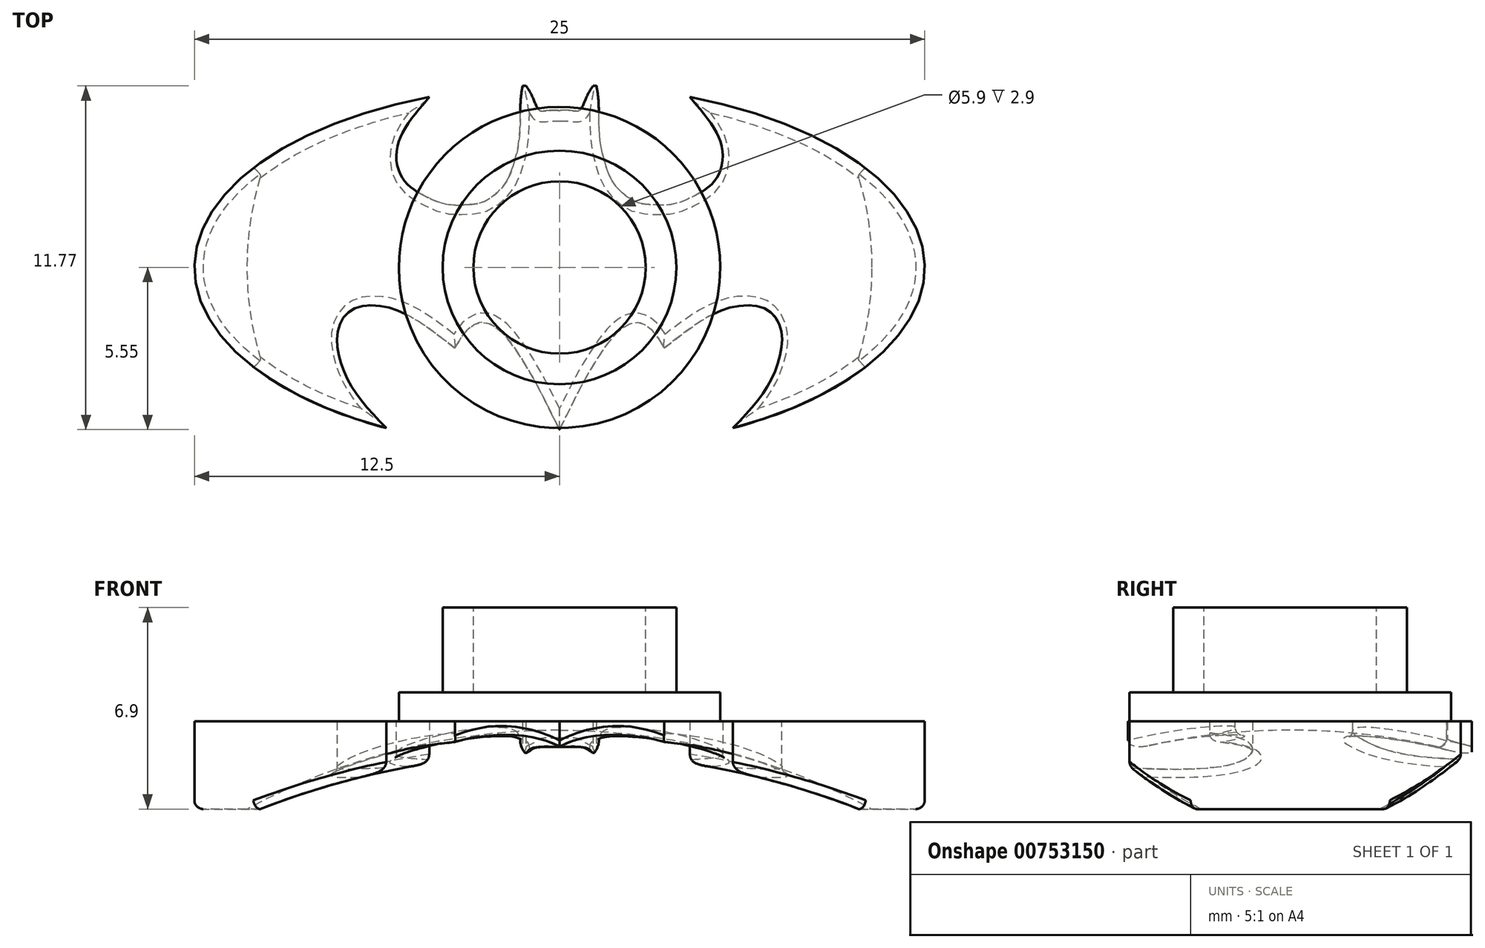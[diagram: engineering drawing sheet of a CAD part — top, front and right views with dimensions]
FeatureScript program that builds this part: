
annotation { "Feature Type Name" : "Feature", "Feature Type Description" : "" }
export const myFeature = defineFeature(function(context is Context, id is Id, definition is map)
    precondition{}
    {
        {
            var Q0;
            Q0=qCreatedBy(makeId("Top.planeOp"),FACE);
            var sketch = newSketch(context, id + "F0", { "sketchPlane" : qUnion([Q0])});
            skEllipticalArc(sketch, "E0", {});
            skFitSpline(sketch, "E1", {"points": [v(-4.46, 5.84) * mm, v(-5.29, 4.77) * mm, v(-5.59, 3.8) * mm, v(-5.32, 2.98) * mm, v(-4.7, 2.5) * mm, v(-3.86, 2.16) * mm, v(-3.2, 2.15) * mm, v(-2.63, 2.24) * mm, v(-1.92, 2.79) * mm, v(-1.58, 3.51) * mm, v(-1.38, 4.44) * mm, v(-1.34, 5.49) * mm, v(-1.26, 6.22) * mm], "startDerivative": vector(-6.9, -8.46) * mm, "endDerivative": vector(1.94, 8.78) * mm});
            skLineSegment(sketch, "E2", {"start": v(0, 0) * mm, "end": v(0, 8.48) * mm, "construction": true});
            skFitSpline(sketch, "E3", {"points": [v(-1.15, 6.22) * mm, v(-0.95, 5.9) * mm, v(-0.8, 5.56) * mm, v(-0.66, 5.36) * mm, v(-0.5, 5.36) * mm, v(-0.24, 5.38) * mm, v(0, 5.38) * mm], "startDerivative": vector(1, -1.46) * mm, "endDerivative": vector(2.36, 0) * mm});
            skLineSegment(sketch, "E4", {"start": v(0, 5.38) * mm, "end": v(0.24, 5.38) * mm, "construction": true});
            skFitSpline(sketch, "E5", {"points": [v(-5.93, -5.5) * mm, v(-6.91, -4.39) * mm, v(-7.47, -3.28) * mm, v(-7.59, -2.16) * mm, v(-7.04, -1.41) * mm, v(-5.77, -1.4) * mm, v(-4.58, -2.01) * mm, v(-3.58, -2.76) * mm], "startDerivative": vector(-6.75, 6.97) * mm, "endDerivative": vector(6.73, -5.3) * mm});
            skFitSpline(sketch, "E6", {"points": [v(0, -5.55) * mm, v(-0.77, -4.02) * mm, v(-1.45, -2.9) * mm, v(-2.1, -2.12) * mm, v(-2.72, -1.88) * mm, v(-3.26, -2.25) * mm, v(-3.58, -2.76) * mm], "startDerivative": vector(-5.35, 10.36) * mm, "endDerivative": vector(-3.6, -5.84) * mm});
            skFitSpline(sketch, "E7.MirrorCS", {"points": [v(4.46, 5.84) * mm, v(5.29, 4.77) * mm, v(5.59, 3.8) * mm, v(5.32, 2.98) * mm, v(4.7, 2.5) * mm, v(3.86, 2.16) * mm, v(3.2, 2.15) * mm, v(2.63, 2.24) * mm, v(1.92, 2.79) * mm, v(1.58, 3.51) * mm, v(1.38, 4.44) * mm, v(1.34, 5.49) * mm, v(1.26, 6.22) * mm], "startDerivative": vector(6.9, -8.46) * mm, "endDerivative": vector(-1.94, 8.78) * mm});
            skFitSpline(sketch, "E8.MirrorCS", {"points": [v(5.93, -5.5) * mm, v(6.91, -4.39) * mm, v(7.47, -3.28) * mm, v(7.59, -2.16) * mm, v(7.04, -1.41) * mm, v(5.77, -1.4) * mm, v(4.58, -2.01) * mm, v(3.58, -2.76) * mm], "startDerivative": vector(6.75, 6.97) * mm, "endDerivative": vector(-6.73, -5.3) * mm});
            skFitSpline(sketch, "E9.MirrorCS", {"points": [v(0, -5.55) * mm, v(0.77, -4.02) * mm, v(1.45, -2.9) * mm, v(2.1, -2.12) * mm, v(2.72, -1.88) * mm, v(3.26, -2.25) * mm, v(3.58, -2.76) * mm], "startDerivative": vector(5.35, 10.36) * mm, "endDerivative": vector(3.6, -5.84) * mm});
            skFitSpline(sketch, "E10.MirrorCS", {"points": [v(1.15, 6.22) * mm, v(0.95, 5.9) * mm, v(0.8, 5.56) * mm, v(0.66, 5.36) * mm, v(0.5, 5.36) * mm, v(0.24, 5.38) * mm, v(0, 5.38) * mm], "startDerivative": vector(-1, -1.46) * mm, "endDerivative": vector(-2.36, 0) * mm});
            skEllipticalArc(sketch, "E11.trimOffspring", {});
            skEllipticalArc(sketch, "E12.trimOffspring", {});
            skEllipticalArc(sketch, "E13.trimOffspring", {});
            const initialGuessF0  = {"E0": [0, 0, -1, 0, 0.0125, 0.00625, 5.077389266040888, 1.0763558123623582], "E11.trimOffspring": [0, 0, -1, 0, 0.0125, 0.00625, 4.804351116669659, 4.8136842039548124], "E12.trimOffspring": [0, 0, -1, 0, 0.0125, 0.00625, 4.611093756814567, 4.62042684409972], "E13.trimOffspring": [0, 0, -1, 0, 0.0125, 0.00625, 2.065236841227435, 4.34738869472849]};
            skSetInitialGuess(sketch, initialGuessF0);
            skSolve(sketch);
        }
        {
            var Q0;
            Q0 = qSketchRegion(id + "F0", true);
            extrude(context, id + "F1", {"entities" : qUnion([Q0]), "depth" : 3 * mm, "offsetDistance" : 25 * mm});
        }
        {
            var Q0;
            Q0=qCreatedBy(makeId("Front.planeOp"),FACE);
            var sketch = newSketch(context, id + "F2", { "sketchPlane" : qUnion([Q0])});
            skLineSegment(sketch, "E14", {"start": v(0, 0) * mm, "end": v(0, -4.5) * mm, "construction": true});
            skSolve(sketch);
        }
        {
            var Q0;
            Q0=qCreatedBy(makeId("Front.planeOp"),FACE);
            var sketch = newSketch(context, id + "F3", { "sketchPlane" : qUnion([Q0])});
            skArc(sketch, "E15", {"start": v(0, 2.7) * mm, "mid": v(-22.55, -19.85) * mm, "end": v(0, -42.4) * mm});
            skLineSegment(sketch, "E16", {"start": v(0, 2.7) * mm, "end": v(0, -42.4) * mm});
            skPoint(sketch, "E17", {"position": v(-10.7, 0) * mm});
            skSolve(sketch);
        }
        {
            var Q0;
            Q0 = qSketchRegion(id + "F3", true);
            var Q1;
            Q1=sQuery(id+"F3.wireOp",EDGE,"E16");
            revolve(context, id + "F4", {"operationType" : NewBodyOperationType.REMOVE, "surfaceOperationType" : NewSurfaceOperationType.NEW, "entities" : qUnion([Q0]), "axis" : qUnion([Q1]), "revolveType" : RevolveType.FULL, "oppositeDirection" : true});
        }
        {
            var Q0;
            Q0=makeQuery(id+"F1.opExtrude","CAP_FACE",FACE,{"disambiguationData":[OSD([sQuery(id+"F0.wireOp",EDGE,"E0"),sQuery(id+"F0.wireOp",EDGE,"E1"),sQuery(id+"F0.wireOp",EDGE,"E3"),sQuery(id+"F0.wireOp",EDGE,"E5"),sQuery(id+"F0.wireOp",EDGE,"E6"),sQuery(id+"F0.wireOp",EDGE,"E7.MirrorCS"),sQuery(id+"F0.wireOp",EDGE,"E8.MirrorCS"),sQuery(id+"F0.wireOp",EDGE,"E9.MirrorCS"),sQuery(id+"F0.wireOp",EDGE,"E10.MirrorCS"),sQuery(id+"F0.wireOp",EDGE,"E11.trimOffspring"),sQuery(id+"F0.wireOp",EDGE,"E12.trimOffspring"),sQuery(id+"F0.wireOp",EDGE,"E13.trimOffspring")])],"isStart":false});
            var sketch = newSketch(context, id + "F5", { "sketchPlane" : qUnion([Q0])});
            skCircle(sketch, "E18", {"center": v(0, 0) * mm, "radius": 5.5 * mm});
            skSolve(sketch);
        }
        {
            var Q0;
            Q0 = qSketchRegion(id + "F5", true);
            extrude(context, id + "F6", {"entities" : qUnion([Q0]), "operationType" : NewBodyOperationType.ADD, "depth" : 1 * mm, "offsetDistance" : 25 * mm});
        }
        {
            var Q0;
            Q0=makeQuery(id+"F6.opExtrude","CAP_FACE",FACE,{"disambiguationData":[OSD([sQuery(id+"F5.wireOp",EDGE,"E18")])],"isStart":false});
            var sketch = newSketch(context, id + "F7", { "sketchPlane" : qUnion([Q0])});
            skCircle(sketch, "E19", {"center": v(0, 0) * mm, "radius": 4 * mm});
            skSolve(sketch);
        }
        {
            var Q0;
            Q0 = qSketchRegion(id + "F7", true);
            extrude(context, id + "F8", {"entities" : qUnion([Q0]), "operationType" : NewBodyOperationType.ADD, "depth" : 2.9 * mm, "offsetDistance" : 25 * mm});
        }
        {
            var Q0;
            Q0=makeQuery(id+"F8.opExtrude","CAP_FACE",FACE,{"disambiguationData":[OSD([sQuery(id+"F7.wireOp",EDGE,"E19")])],"isStart":false});
            var sketch = newSketch(context, id + "F9", { "sketchPlane" : qUnion([Q0])});
            skCircle(sketch, "E20", {"center": v(0, 0) * mm, "radius": 2.95 * mm});
            skSolve(sketch);
        }
        {
            var Q0;
            Q0 = qSketchRegion(id + "F9", true);
            extrude(context, id + "F10", {"entities" : qUnion([Q0]), "operationType" : NewBodyOperationType.REMOVE, "oppositeDirection" : true, "depth" : 2.9 * mm, "offsetDistance" : 25 * mm});
        }
        {
            var Q0;
            Q0=makeQuery(id+"F1.opExtrude","CAP_EDGE",EDGE,{"disambiguationData":[OSD([sQuery(id+"F0.wireOp",EDGE,"E13.trimOffspring")])],"isStart":true});
            var Q1;
            Q1=makeQuery(id+"F4.boolean.opBoolean","INTERSECT",EDGE,{"disambiguationData":[OD(0.0)],"derivedFrom":[makeQuery(id+"F1.opExtrude","SWEPT_FACE",FACE,{"disambiguationData":[OSD([sQuery(id+"F0.wireOp",EDGE,"E13.trimOffspring")])]}),makeQuery(id+"F4.opRevolve","SWEPT_FACE",FACE,{"disambiguationData":[OSD([sQuery(id+"F3.wireOp",EDGE,"E15")])]})]});
            var Q2;
            Q2=makeQuery(id+"F4.boolean.opBoolean","INTERSECT",EDGE,{"disambiguationData":[OD(1.0)],"derivedFrom":[makeQuery(id+"F1.opExtrude","SWEPT_FACE",FACE,{"disambiguationData":[OSD([sQuery(id+"F0.wireOp",EDGE,"E13.trimOffspring")])]}),makeQuery(id+"F4.opRevolve","SWEPT_FACE",FACE,{"disambiguationData":[OSD([sQuery(id+"F3.wireOp",EDGE,"E15")])]})]});
            var Q3;
            Q3=makeQuery(id+"F4.boolean.opBoolean","INTERSECT",EDGE,{"disambiguationData":[OD(1.0)],"derivedFrom":[makeQuery(id+"F1.opExtrude","SWEPT_FACE",FACE,{"disambiguationData":[OSD([sQuery(id+"F0.wireOp",EDGE,"E0")])]}),makeQuery(id+"F4.opRevolve","SWEPT_FACE",FACE,{"disambiguationData":[OSD([sQuery(id+"F3.wireOp",EDGE,"E15")])]})]});
            var Q4;
            Q4=makeQuery(id+"F1.opExtrude","CAP_EDGE",EDGE,{"disambiguationData":[OSD([sQuery(id+"F0.wireOp",EDGE,"E0")])],"isStart":true});
            var Q5;
            Q5=makeQuery(id+"F4.boolean.opBoolean","INTERSECT",EDGE,{"disambiguationData":[OD(0.0)],"derivedFrom":[makeQuery(id+"F1.opExtrude","SWEPT_FACE",FACE,{"disambiguationData":[OSD([sQuery(id+"F0.wireOp",EDGE,"E0")])]}),makeQuery(id+"F4.opRevolve","SWEPT_FACE",FACE,{"disambiguationData":[OSD([sQuery(id+"F3.wireOp",EDGE,"E15")])]})]});
            var Q6;
            Q6=makeQuery(id+"F4.boolean.opBoolean","INTERSECT",EDGE,{"derivedFrom":[makeQuery(id+"F1.opExtrude","SWEPT_FACE",FACE,{"disambiguationData":[OSD([sQuery(id+"F0.wireOp",EDGE,"E5")])]}),makeQuery(id+"F4.opRevolve","SWEPT_FACE",FACE,{"disambiguationData":[OSD([sQuery(id+"F3.wireOp",EDGE,"E15")])]})]});
            var Q7;
            Q7=makeQuery(id+"F4.boolean.opBoolean","INTERSECT",EDGE,{"derivedFrom":[makeQuery(id+"F1.opExtrude","SWEPT_FACE",FACE,{"disambiguationData":[OSD([sQuery(id+"F0.wireOp",EDGE,"E6")])]}),makeQuery(id+"F4.opRevolve","SWEPT_FACE",FACE,{"disambiguationData":[OSD([sQuery(id+"F3.wireOp",EDGE,"E15")])]})]});
            var Q8;
            Q8=makeQuery(id+"F4.boolean.opBoolean","INTERSECT",EDGE,{"derivedFrom":[makeQuery(id+"F1.opExtrude","SWEPT_FACE",FACE,{"disambiguationData":[OSD([sQuery(id+"F0.wireOp",EDGE,"E9.MirrorCS")])]}),makeQuery(id+"F4.opRevolve","SWEPT_FACE",FACE,{"disambiguationData":[OSD([sQuery(id+"F3.wireOp",EDGE,"E15")])]})]});
            var Q9;
            Q9=makeQuery(id+"F4.boolean.opBoolean","INTERSECT",EDGE,{"derivedFrom":[makeQuery(id+"F1.opExtrude","SWEPT_FACE",FACE,{"disambiguationData":[OSD([sQuery(id+"F0.wireOp",EDGE,"E8.MirrorCS")])]}),makeQuery(id+"F4.opRevolve","SWEPT_FACE",FACE,{"disambiguationData":[OSD([sQuery(id+"F3.wireOp",EDGE,"E15")])]})]});
            var Q10;
            Q10=makeQuery(id+"F4.boolean.opBoolean","INTERSECT",EDGE,{"derivedFrom":[makeQuery(id+"F1.opExtrude","SWEPT_FACE",FACE,{"disambiguationData":[OSD([sQuery(id+"F0.wireOp",EDGE,"E7.MirrorCS")])]}),makeQuery(id+"F4.opRevolve","SWEPT_FACE",FACE,{"disambiguationData":[OSD([sQuery(id+"F3.wireOp",EDGE,"E15")])]})]});
            var Q11;
            Q11=makeQuery(id+"F4.boolean.opBoolean","INTERSECT",EDGE,{"derivedFrom":[makeQuery(id+"F1.opExtrude","SWEPT_FACE",FACE,{"disambiguationData":[OSD([sQuery(id+"F0.wireOp",EDGE,"E1")])]}),makeQuery(id+"F4.opRevolve","SWEPT_FACE",FACE,{"disambiguationData":[OSD([sQuery(id+"F3.wireOp",EDGE,"E15")])]})]});
            var Q12;
            Q12=makeQuery(id+"F4.boolean.opBoolean","INTERSECT",EDGE,{"derivedFrom":[makeQuery(id+"F1.opExtrude","SWEPT_FACE",FACE,{"disambiguationData":[OSD([sQuery(id+"F0.wireOp",EDGE,"E10.MirrorCS")])]}),makeQuery(id+"F4.opRevolve","SWEPT_FACE",FACE,{"disambiguationData":[OSD([sQuery(id+"F3.wireOp",EDGE,"E15")])]})]});
            fillet(context, id + "F11", {"entities" : qUnion([Q0, Q1, Q2, Q3, Q4, Q5, Q6, Q7, Q8, Q9, Q10, Q11, Q12]), "radius" : 0.3 * mm, "tangentPropagation" : true, "allowEdgeOverflow" : false});
        }
    });
